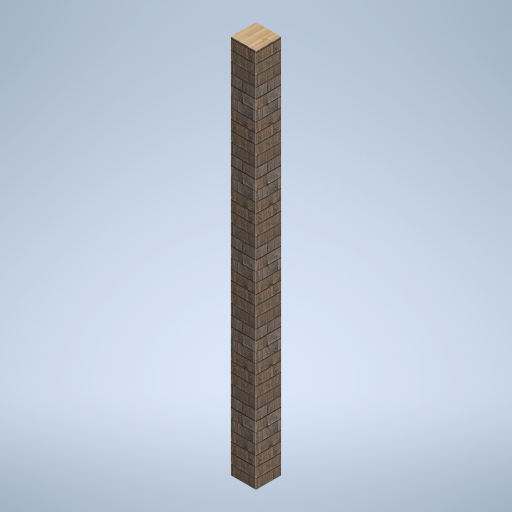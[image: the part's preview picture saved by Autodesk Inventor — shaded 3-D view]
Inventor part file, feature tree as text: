
AUTODESK INVENTOR PART (.ipt)
format: ipt  version: 2024.2 (Build 282272000, 272)  size: 312,320 bytes
history: native  units: in
note: dims shown in document units (in); Inventor stores cm internally (conversion verified against a paired STEP export)
features: other x3, sketch x1
ambient origin geometry x8: Origin, YZ Plane, XZ Plane, XY Plane, X Axis, Y Axis, Z Axis, Center Point
bodies: Solid1 (feature_tree)
feature tree (4):
  other  "support_frame_03.ipt"
  other  "Solid1::support_frame_03.ipt"
  other  "TaggingFeature1"
  sketch  "Sketch1"  dims[d0=0.3937in]
